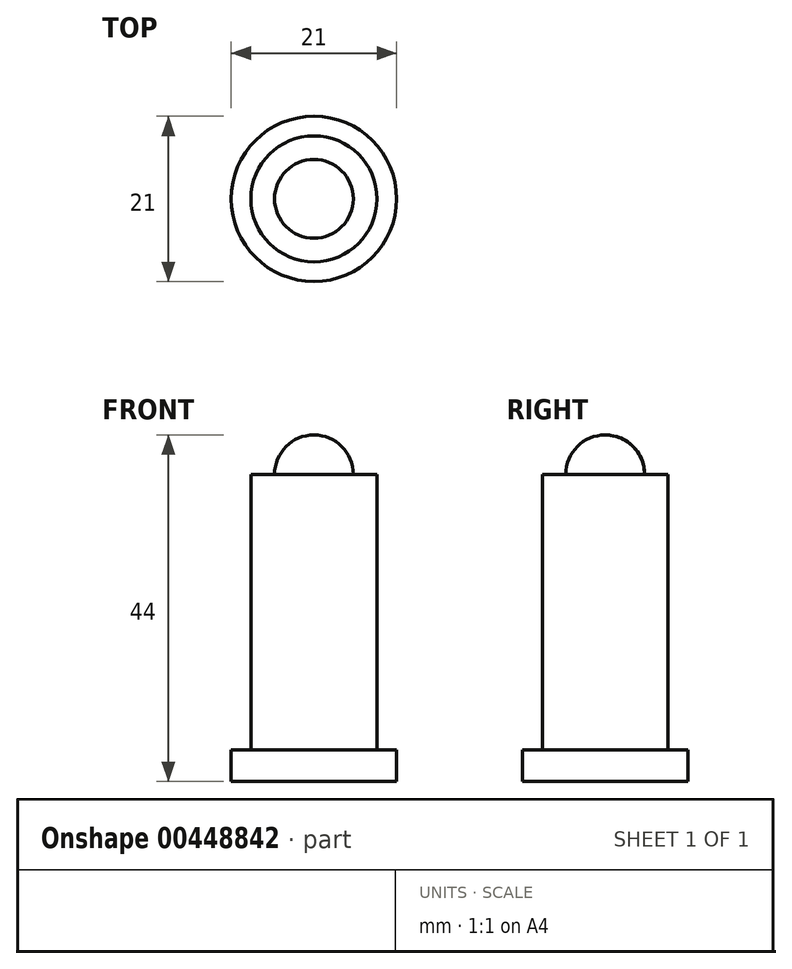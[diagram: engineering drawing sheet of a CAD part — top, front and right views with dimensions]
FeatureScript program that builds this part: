
annotation { "Feature Type Name" : "Feature", "Feature Type Description" : "" }
export const myFeature = defineFeature(function(context is Context, id is Id, definition is map)
    precondition{}
    {
        {
            var Q0;
            Q0=qCreatedBy(makeId("Top.planeOp"),FACE);
            var sketch = newSketch(context, id + "F0", { "sketchPlane" : qUnion([Q0])});
            skCircle(sketch, "E0", {"center": v(0, 0) * mm, "radius": 10.5 * mm});
            skSolve(sketch);
        }
        {
            var Q0;
            Q0=qSketchRegion(id+"F0",true);
            extrude(context, id + "F1", {"entities" : qUnion([Q0]), "depth" : 4 * mm});
        }
        {
            var Q0;
            Q0=qCreatedBy(makeId("Top.planeOp"),FACE);
            var sketch = newSketch(context, id + "F2", { "sketchPlane" : qUnion([Q0])});
            skCircle(sketch, "E1", {"center": v(0, 0) * mm, "radius": 8 * mm});
            skSolve(sketch);
        }
        {
            var Q0;
            Q0=qSketchRegion(id+"F2",true);
            extrude(context, id + "F3", {"entities" : qUnion([Q0]), "operationType" : NewBodyOperationType.ADD, "depth" : 39 * mm});
        }
        {
            var Q0;
            Q0=qCreatedBy(makeId("Right.planeOp"),FACE);
            var sketch = newSketch(context, id + "F4", { "sketchPlane" : qUnion([Q0])});
            skLineSegment(sketch, "E2", {"start": v(0, 44) * mm, "end": v(0, 39) * mm});
            skLineSegment(sketch, "E3", {"start": v(0, 39) * mm, "end": v(5, 39) * mm});
            skArc(sketch, "E4", {"start": v(5, 39) * mm, "mid": v(3.54, 42.54) * mm, "end": v(0, 44) * mm});
            skSolve(sketch);
        }
        {
            var Q0;
            Q0=makeQuery(id+"F4.imprint","IMPRINT",FACE,{"disambiguationData":[TD([[makeQuery(id+"F4.imprint","IMPRINT",EDGE,{"derivedFrom":sQuery(id+"F4.wireOp",EDGE,"E2")}),1.0]])]});
            var Q1;
            Q1=sQuery(id+"F4.wireOp",EDGE,"E2");
            revolve(context, id + "F5", {"operationType" : NewBodyOperationType.ADD, "entities" : qUnion([Q0]), "axis" : qUnion([Q1]), "revolveType" : RevolveType.FULL});
        }
    });
